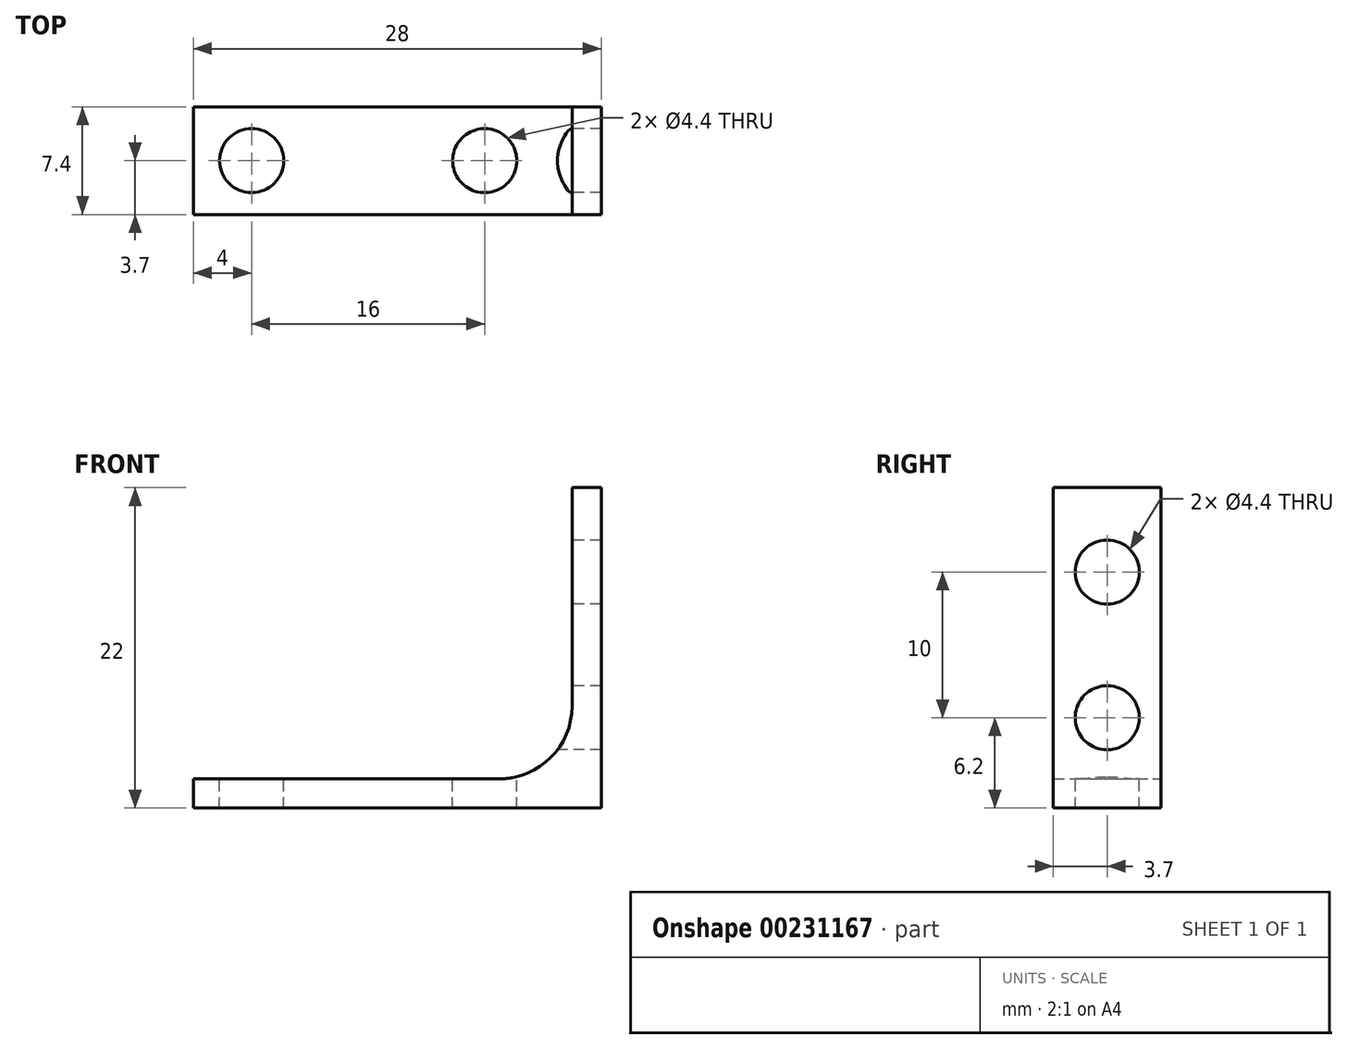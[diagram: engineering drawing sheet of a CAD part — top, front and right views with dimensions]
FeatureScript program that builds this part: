
annotation { "Feature Type Name" : "Feature", "Feature Type Description" : "" }
export const myFeature = defineFeature(function(context is Context, id is Id, definition is map)
    precondition{}
    {
        {
            var Q0;
            Q0=qCreatedBy(makeId("Top.planeOp"),FACE);
            var sketch = newSketch(context, id + "F0", { "sketchPlane" : qUnion([Q0])});
            skLineSegment(sketch, "E0.bottom", {"start": v(-28, 0) * mm, "end": v(0, 0) * mm});
            skLineSegment(sketch, "E0.top", {"start": v(-28, -7.4) * mm, "end": v(0, -7.4) * mm});
            skLineSegment(sketch, "E0.left", {"start": v(-28, 0) * mm, "end": v(-28, -7.4) * mm});
            skLineSegment(sketch, "E0.right", {"start": v(0, 0) * mm, "end": v(0, -7.4) * mm});
            skSolve(sketch);
        }
        {
            var Q0;
            Q0 = qSketchRegion(id + "F0", true);
            extrude(context, id + "F1", {"entities" : qUnion([Q0]), "depth" : 22 * mm});
        }
        {
            var Q0;
            Q0=makeQuery(id+"F1.opExtrude","CAP_FACE",FACE,{"disambiguationData":[OSD([sQuery(id+"F0.wireOp",EDGE,"E0.bottom"),sQuery(id+"F0.wireOp",EDGE,"E0.top"),sQuery(id+"F0.wireOp",EDGE,"E0.left"),sQuery(id+"F0.wireOp",EDGE,"E0.right")])],"isStart":false});
            var sketch = newSketch(context, id + "F2", { "sketchPlane" : qUnion([Q0])});
            skPoint(sketch, "E1", {"position": v(-24, -3.7) * mm});
            skPoint(sketch, "E2", {"position": v(-8, -3.7) * mm});
            skSolve(sketch);
        }
        {
            var Q0;
            Q0=sQuery(id+"F2.wireOp",VERTEX,"eb8f697e-f6a5-44ec-9cfb-51c459bbc202");
            var Q1;
            Q1=sQuery(id+"F2.wireOp",VERTEX,"f4fb2278-768e-476d-9ba5-1fd1232f0111");
            var Q2;
            Q2=sQuery(id+"F2.wireOp",VERTEX,"E1");
            var Q3;
            Q3=sQuery(id+"F2.wireOp",VERTEX,"E2");
            var Q4;
            Q4=makeQuery(id+"F1.opExtrude","SWEPT_BODY",BODY,{"disambiguationData":[OSD([sQuery(id+"F0.wireOp",EDGE,"E0.bottom"),sQuery(id+"F0.wireOp",EDGE,"E0.top"),sQuery(id+"F0.wireOp",EDGE,"E0.left"),sQuery(id+"F0.wireOp",EDGE,"E0.right")])]});
            hole(context, id + "F3", {"style" : HoleStyle.SIMPLE, "endStyle" : HoleEndStyle.THROUGH, "standardTappedOrClearance" : lookupTablePath({ "standard" : "ISO", "fit" : "Normal", "size" : "M4", "type" : "Clearance" }), "standardBlindInLast" : lookupTablePath({ "fit" : "Standard", "standard" : "ISO", "size" : "M4", "type" : "Clearance" }), "holeDiameter" : 4.4 * mm, "isTappedThrough" : true, "tappedDepth" : 12 * mm, "tapClearance" : 3, "locations" : qUnion([Q0, Q1, Q2, Q3]), "scope" : qUnion([Q4])});
        }
        {
            var Q0;
            Q0=makeQuery(id+"F1.opExtrude","SWEPT_FACE",FACE,{"disambiguationData":[OSD([sQuery(id+"F0.wireOp",EDGE,"E0.bottom")])]});
            var sketch = newSketch(context, id + "F4", { "sketchPlane" : qUnion([Q0])});
            skLineSegment(sketch, "E3.bottom", {"start": v(2, 22) * mm, "end": v(28, 22) * mm});
            skLineSegment(sketch, "E3.top", {"start": v(2, 2) * mm, "end": v(28, 2) * mm});
            skLineSegment(sketch, "E3.left", {"start": v(2, 22) * mm, "end": v(2, 2) * mm});
            skLineSegment(sketch, "E3.right", {"start": v(28, 22) * mm, "end": v(28, 2) * mm});
            skSolve(sketch);
        }
        {
            var Q0;
            Q0 = qSketchRegion(id + "F4", true);
            extrude(context, id + "F5", {"entities" : qUnion([Q0]), "operationType" : NewBodyOperationType.REMOVE, "oppositeDirection" : true, "depth" : 25 * mm});
        }
        {
            var Q0;
            Q0=makeQuery(id+"F5.boolean.opBoolean","COPY",FACE,{"derivedFrom":makeQuery(id+"F5.opExtrude","SWEPT_FACE",FACE,{"disambiguationData":[OSD([sQuery(id+"F4.wireOp",EDGE,"E3.left")])]})});
            var sketch = newSketch(context, id + "F6", { "sketchPlane" : qUnion([Q0])});
            skPoint(sketch, "E4", {"position": v(3.7, 6.2) * mm});
            skPoint(sketch, "E5", {"position": v(3.7, 16.2) * mm});
            skSolve(sketch);
        }
        {
            var Q0;
            Q0=sQuery(id+"F6.wireOp",VERTEX,"E5");
            var Q1;
            Q1=sQuery(id+"F6.wireOp",VERTEX,"E4");
            var Q2;
            Q2=makeQuery(id+"F1.opExtrude","SWEPT_BODY",BODY,{"disambiguationData":[OSD([sQuery(id+"F0.wireOp",EDGE,"E0.bottom"),sQuery(id+"F0.wireOp",EDGE,"E0.top"),sQuery(id+"F0.wireOp",EDGE,"E0.left"),sQuery(id+"F0.wireOp",EDGE,"E0.right")])]});
            hole(context, id + "F7", {"style" : HoleStyle.SIMPLE, "endStyle" : HoleEndStyle.THROUGH, "standardTappedOrClearance" : lookupTablePath({ "standard" : "ISO", "fit" : "Normal", "size" : "M4", "type" : "Clearance" }), "standardBlindInLast" : lookupTablePath({ "fit" : "Standard", "standard" : "ISO", "size" : "M4", "type" : "Clearance" }), "holeDiameter" : 4.4 * mm, "isTappedThrough" : true, "tappedDepth" : 12 * mm, "tapClearance" : 3, "locations" : qUnion([Q0, Q1]), "scope" : qUnion([Q2])});
        }
        {
            var Q0;
            Q0=makeQuery(id+"F5.boolean.opBoolean","COPY",EDGE,{"derivedFrom":makeQuery(id+"F5.opExtrude","SWEPT_EDGE",EDGE,{"disambiguationData":[OSD([sQuery(id+"F4.wireOp",EDGE,"E3.top"),sQuery(id+"F4.wireOp",EDGE,"E3.left")])]})});
            fillet(context, id + "F8", {"entities" : qUnion([Q0]), "radius" : 5 * mm, "tangentPropagation" : true, "allowEdgeOverflow" : false});
        }
    });
